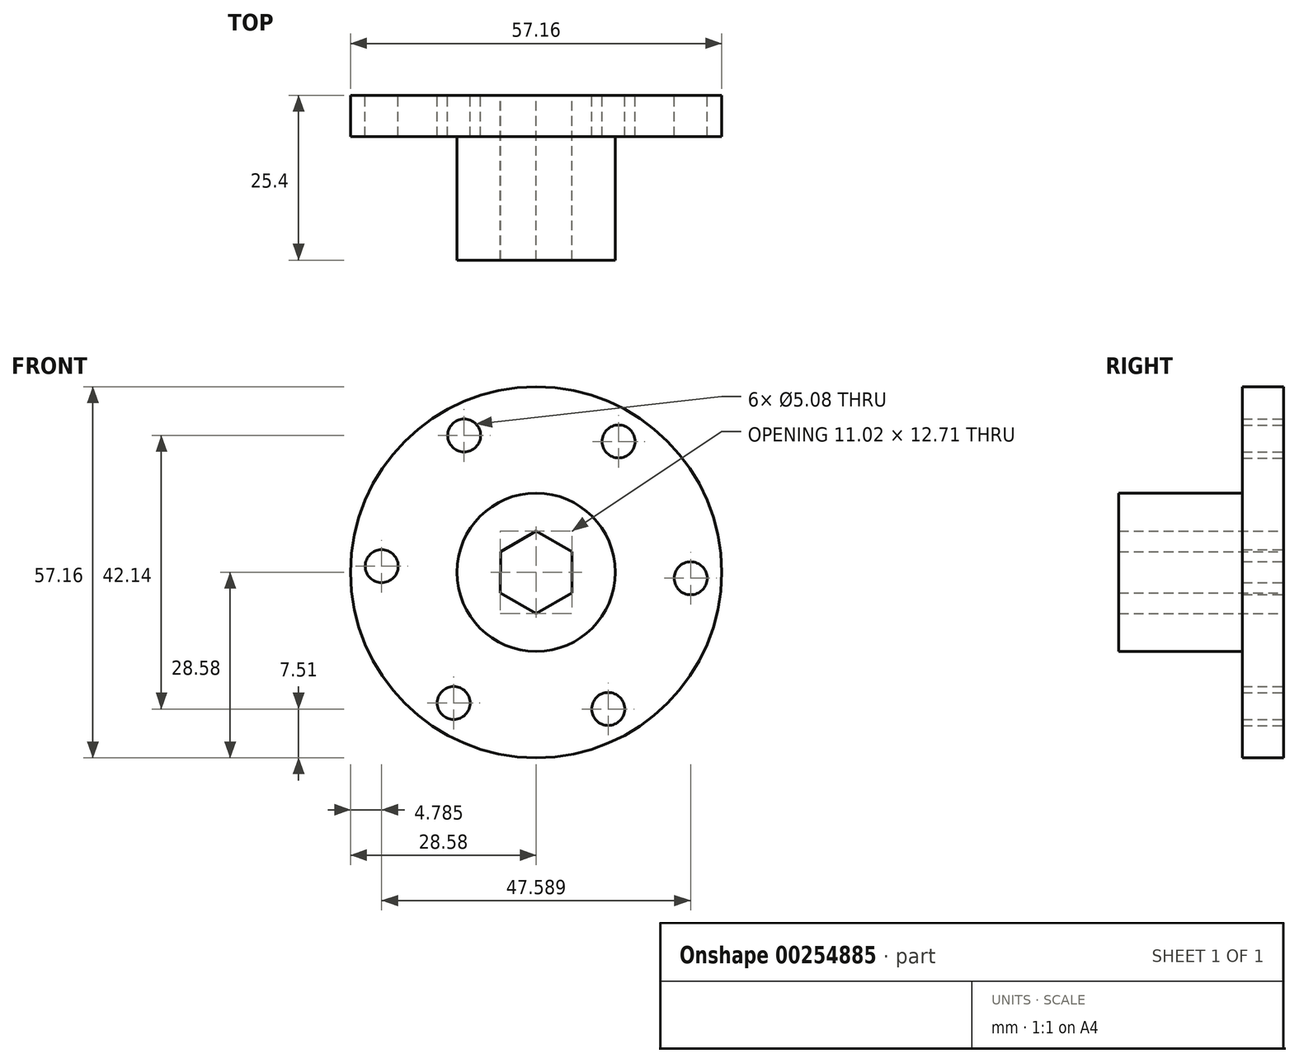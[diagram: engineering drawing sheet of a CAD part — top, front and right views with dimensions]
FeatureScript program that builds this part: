
annotation { "Feature Type Name" : "Feature", "Feature Type Description" : "" }
export const myFeature = defineFeature(function(context is Context, id is Id, definition is map)
    precondition{}
    {
        {
            var Q0;
            Q0=qCreatedBy(makeId("Front.planeOp"),FACE);
            var sketch = newSketch(context, id + "F0", { "sketchPlane" : qUnion([Q0])});
            skCircle(sketch, "E0", {"center": v(0, 0) * mm, "radius": 28.58 * mm});
            skCircle(sketch, "E1", {"center": v(12.7, 20.14) * mm, "radius": 2.54 * mm});
            skCircle(sketch, "E2", {"center": v(23.8, -0.93) * mm, "radius": 2.54 * mm});
            skCircle(sketch, "E3", {"center": v(11.1, -21.07) * mm, "radius": 2.54 * mm});
            skCircle(sketch, "E4", {"center": v(-12.7, -20.14) * mm, "radius": 2.54 * mm});
            skCircle(sketch, "E5", {"center": v(-23.8, 0.93) * mm, "radius": 2.54 * mm});
            skCircle(sketch, "E6", {"center": v(-11.1, 21.07) * mm, "radius": 2.54 * mm});
            skCircle(sketch, "E7", {"center": v(0, 0) * mm, "radius": 12.2 * mm});
            skLineSegment(sketch, "E8.1", {"start": v(0, 6.36) * mm, "end": v(5.51, 3.17) * mm});
            skLineSegment(sketch, "E8.2", {"start": v(5.51, 3.17) * mm, "end": v(5.5, -3.19) * mm});
            skLineSegment(sketch, "E8.3", {"start": v(5.5, -3.19) * mm, "end": v(0, -6.36) * mm});
            skLineSegment(sketch, "E8.4", {"start": v(0, -6.36) * mm, "end": v(-5.51, -3.17) * mm});
            skLineSegment(sketch, "E8.5", {"start": v(-5.51, -3.17) * mm, "end": v(-5.5, 3.19) * mm});
            skLineSegment(sketch, "E9", {"start": v(-5.5, 3.19) * mm, "end": v(0, 6.36) * mm});
            skSolve(sketch);
        }
        {
            var Q0;
            Q0=makeQuery(id+"F0.imprint","IMPRINT",FACE,{"disambiguationData":[TD([[makeQuery(id+"F0.imprint","IMPRINT",EDGE,{"derivedFrom":sQuery(id+"F0.wireOp",EDGE,"E0")}),1.0]])]});
            extrude(context, id + "F1", {"entities" : qUnion([Q0]), "depth" : 6.35 * mm});
        }
        {
            var Q0;
            Q0=makeQuery(id+"F0.imprint","IMPRINT",FACE,{"disambiguationData":[TD([[makeQuery(id+"F0.imprint","IMPRINT",EDGE,{"derivedFrom":sQuery(id+"F0.wireOp",EDGE,"E7")}),1.0]])]});
            extrude(context, id + "F2", {"entities" : qUnion([Q0]), "operationType" : NewBodyOperationType.ADD, "depth" : 25.4 * mm});
        }
    });
